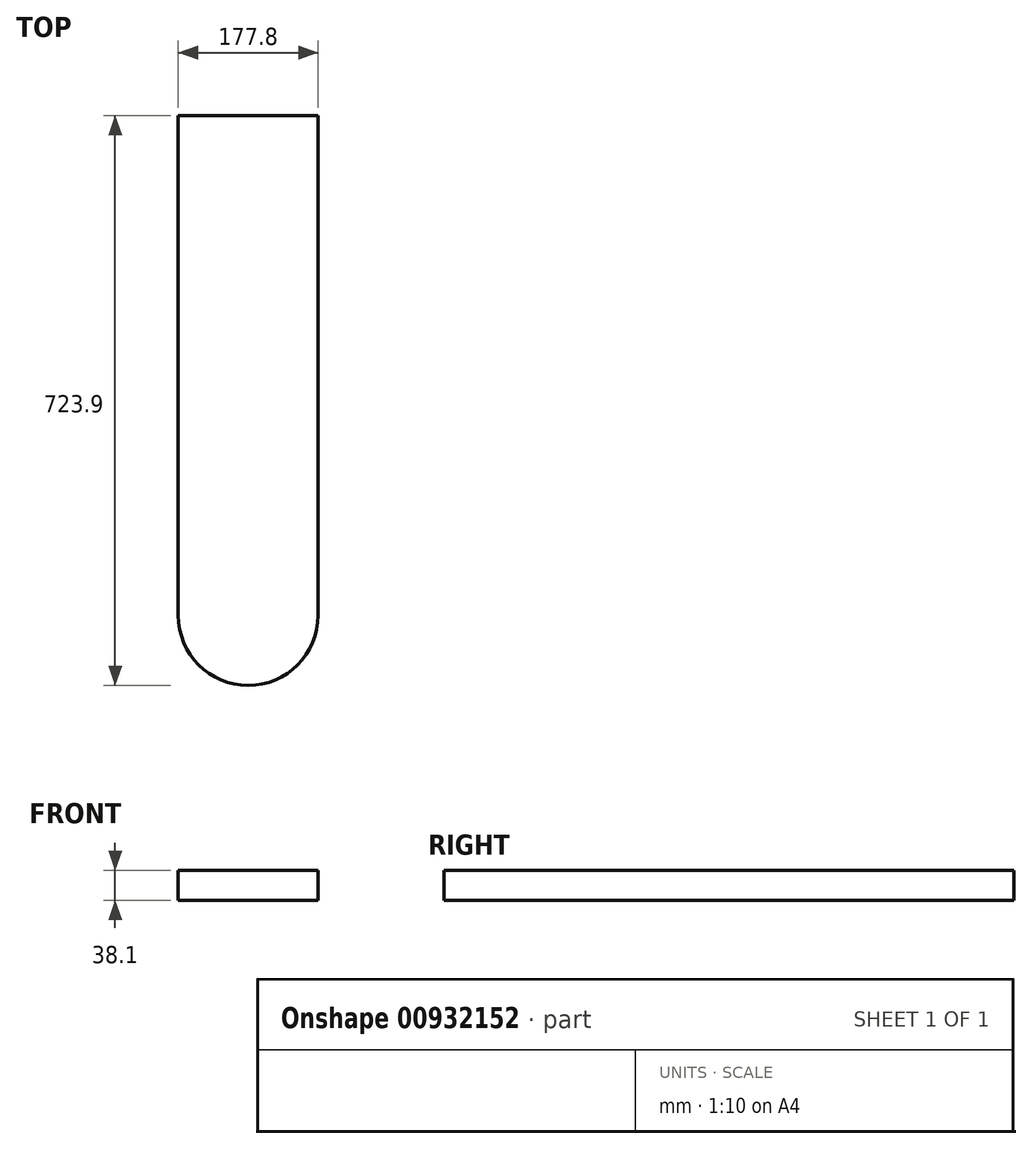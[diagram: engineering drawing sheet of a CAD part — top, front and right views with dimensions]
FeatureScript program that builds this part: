
annotation { "Feature Type Name" : "Feature", "Feature Type Description" : "" }
export const myFeature = defineFeature(function(context is Context, id is Id, definition is map)
    precondition{}
    {
        {
            var Q0;
            Q0=qCreatedBy(makeId("Top.planeOp"),FACE);
            var sketch = newSketch(context, id + "F0", { "sketchPlane" : qUnion([Q0])});
            skLineSegment(sketch, "E0.top", {"start": v(88.9, 317.5) * mm, "end": v(-88.9, 317.5) * mm});
            skLineSegment(sketch, "E0.left", {"start": v(88.9, -317.5) * mm, "end": v(88.9, 317.5) * mm});
            skLineSegment(sketch, "E0.right", {"start": v(-88.9, -317.5) * mm, "end": v(-88.9, 317.5) * mm});
            skPoint(sketch, "E0.middle", {"position": v(0, 0) * mm});
            skArc(sketch, "E1", {"start": v(-88.9, -317.5) * mm, "mid": v(0, -406.4) * mm, "end": v(88.9, -317.5) * mm});
            skSolve(sketch);
        }
        {
            var Q0;
            Q0 = qSketchRegion(id + "F0", true);
            extrude(context, id + "F1", {"entities" : qUnion([Q0]), "depth" : 38.1 * mm, "offsetDistance" : 25.4 * mm});
        }
    });
